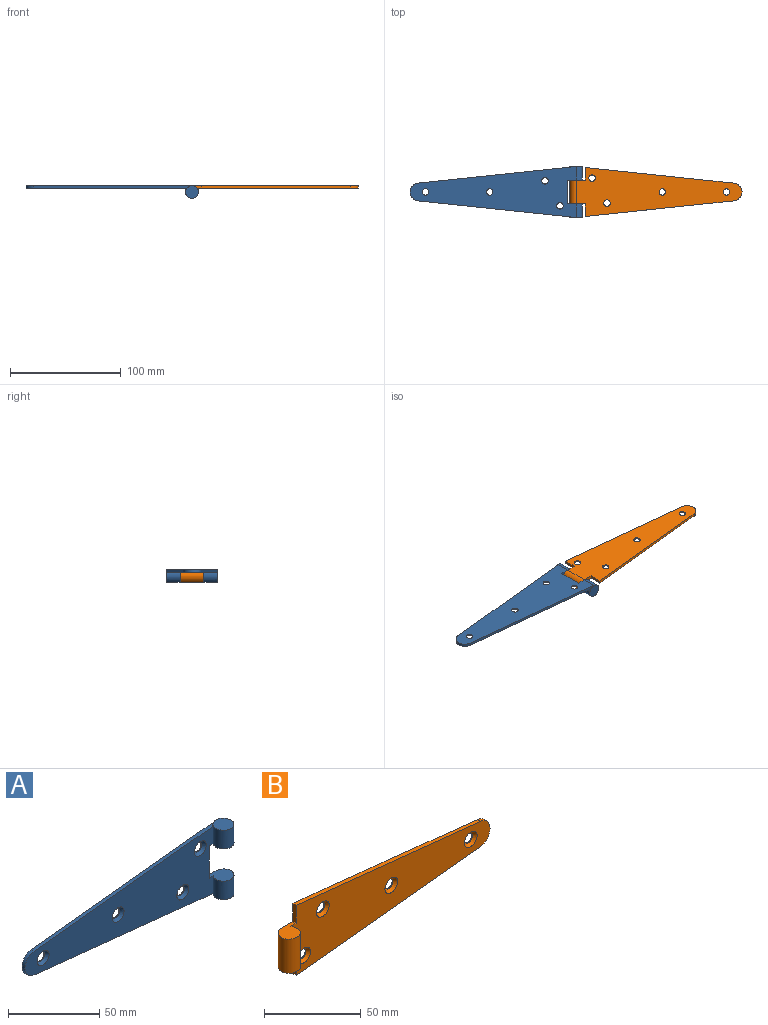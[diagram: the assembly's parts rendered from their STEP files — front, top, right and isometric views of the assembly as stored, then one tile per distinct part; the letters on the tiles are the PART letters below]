
ASSEMBLY  parts=2 mates=1
PART A: 20 faces, bbox 155.8x11.5x46.5 mm
  f0: cylinder r=5.75mm len=12.5mm, axis (0,0,-1), area 387.7mm2, adj f1,f3,f5,f7,f18
  f1: plane 145.4x45.03mm, normal (0,-1,0), area 3965.4mm2, adj f0,f2,f3,f4,f6,f10,f12,f14
  f2: plane 142.84x15.04mm, normal (-0.1,0,-0.99), area 322.9mm2, adj f1,f4,f5,f6
  f3: plane 142.84x15.04mm, normal (-0.1,0,0.99), area 322.9mm2, adj f0,f1,f4,f5
  f4: cylinder r=8mm len=15.91mm, axis (0,-1,0), area 53.9mm2, adj f1,f2,f3,f5
  f5: plane 150x46mm, normal (0,1,0), area 4241.9mm2, adj f0,f2,f3,f4,f6,f9,f11,f13
  f6: cylinder r=5.75mm len=12.5mm, axis (0,0,-1), area 387.7mm2, adj f1,f2,f5,f8,f19
  f7: plane 11.5x11.5mm, normal (0,0,1), area 103.9mm2, adj f0
  f8: plane 11.5x11.5mm, normal (0,0,-1), area 103.9mm2, adj f6
  f9: cylinder r=2.9mm len=5.8mm, axis (0,-1,0), area 10mm2, adj f5,f10
  f10: cone r=2.9mm half-angle=45deg, axis (0,-1,0), area 58.7mm2, adj f1,f9
  f11: cylinder r=2.9mm len=5.8mm, axis (0,-1,0), area 10mm2, adj f5,f12
  f12: cone r=2.9mm half-angle=45deg, axis (0,-1,0), area 58.7mm2, adj f1,f11
  f13: cylinder r=2.9mm len=5.8mm, axis (0,-1,0), area 10mm2, adj f5,f14
  f14: cone r=2.9mm half-angle=45deg, axis (0,-1,0), area 58.7mm2, adj f1,f13
  f15: cylinder r=2.9mm len=5.8mm, axis (0,-1,0), area 10mm2, adj f5,f16
  f16: cone r=2.9mm half-angle=45deg, axis (0,-1,0), area 58.7mm2, adj f1,f15
  f17: plane 21.5x2.3mm, normal (1,0,0), area 49.4mm2, adj f1,f5,f18,f19
  f18: plane 13.25x11.5mm, normal (0,0,-1), area 113.7mm2, adj f0,f1,f5,f17
  f19: plane 13.25x11.5mm, normal (0,0,1), area 113.7mm2, adj f1,f5,f6,f17
PART B: 18 faces, bbox 155.8x11.5x44.2 mm
  f0: plane 14.25x11.5mm, normal (0,0,1), area 116mm2, adj f2,f13,f14,f17
  f1: plane 14.25x11.5mm, normal (0,0,-1), area 116mm2, adj f3,f13,f14,f17
  f2: plane 11.35x2.3mm, normal (-1,0,0), area 26.1mm2, adj f0,f14,f15,f17
  f3: plane 11.35x2.3mm, normal (-1,0,0), area 26.1mm2, adj f1,f14,f16,f17
  f4: cone r=2.9mm half-angle=45deg, axis (0,-1,0), area 58.7mm2, adj f12,f17
  f5: cone r=2.9mm half-angle=45deg, axis (0,-1,0), area 58.7mm2, adj f11,f17
  f6: cone r=2.9mm half-angle=45deg, axis (0,-1,0), area 58.7mm2, adj f10,f17
  f7: cone r=2.9mm half-angle=45deg, axis (0,-1,0), area 58.7mm2, adj f9,f17
  f8: cylinder r=8mm len=15.91mm, axis (0,-1,0), area 53.9mm2, adj f14,f15,f16,f17
  f9: cylinder r=2.9mm len=5.8mm, axis (0,-1,0), area 10mm2, adj f7,f14
  f10: cylinder r=2.9mm len=5.8mm, axis (0,-1,0), area 10mm2, adj f6,f14
  f11: cylinder r=2.9mm len=5.8mm, axis (0,-1,0), area 10mm2, adj f5,f14
  f12: cylinder r=2.9mm len=5.8mm, axis (0,-1,0), area 10mm2, adj f4,f14
  f13: cylinder r=5.75mm len=21.5mm, axis (0,0,-1), area 662.1mm2, adj f0,f1,f14,f17
  f14: plane 150x44.21mm, normal (0,1,0), area 4202.5mm2, adj f0,f1,f2,f3,f8,f9,f10,f11
  f15: plane 134.34x14.15mm, normal (0.1,0,0.99), area 310.7mm2, adj f2,f8,f14,f17
  f16: plane 134.34x14.15mm, normal (0.1,0,-0.99), area 310.7mm2, adj f3,f8,f14,f17
  f17: plane 145.4x44.21mm, normal (0,-1,0), area 3937.6mm2, adj f0,f1,f2,f3,f4,f5,f6,f7
PLACE A rot(axis=(1,0,0),90deg) t=(63.64,-0.02,-2.3)mm
PLACE B rot(axis=(1,0,0),90deg) t=(63.64,-0.02,-2.3)mm
MATE revolute A.f0 <-> B.f13  axis (0,1,0) through (63.64,-10.77,-5.75)mm
